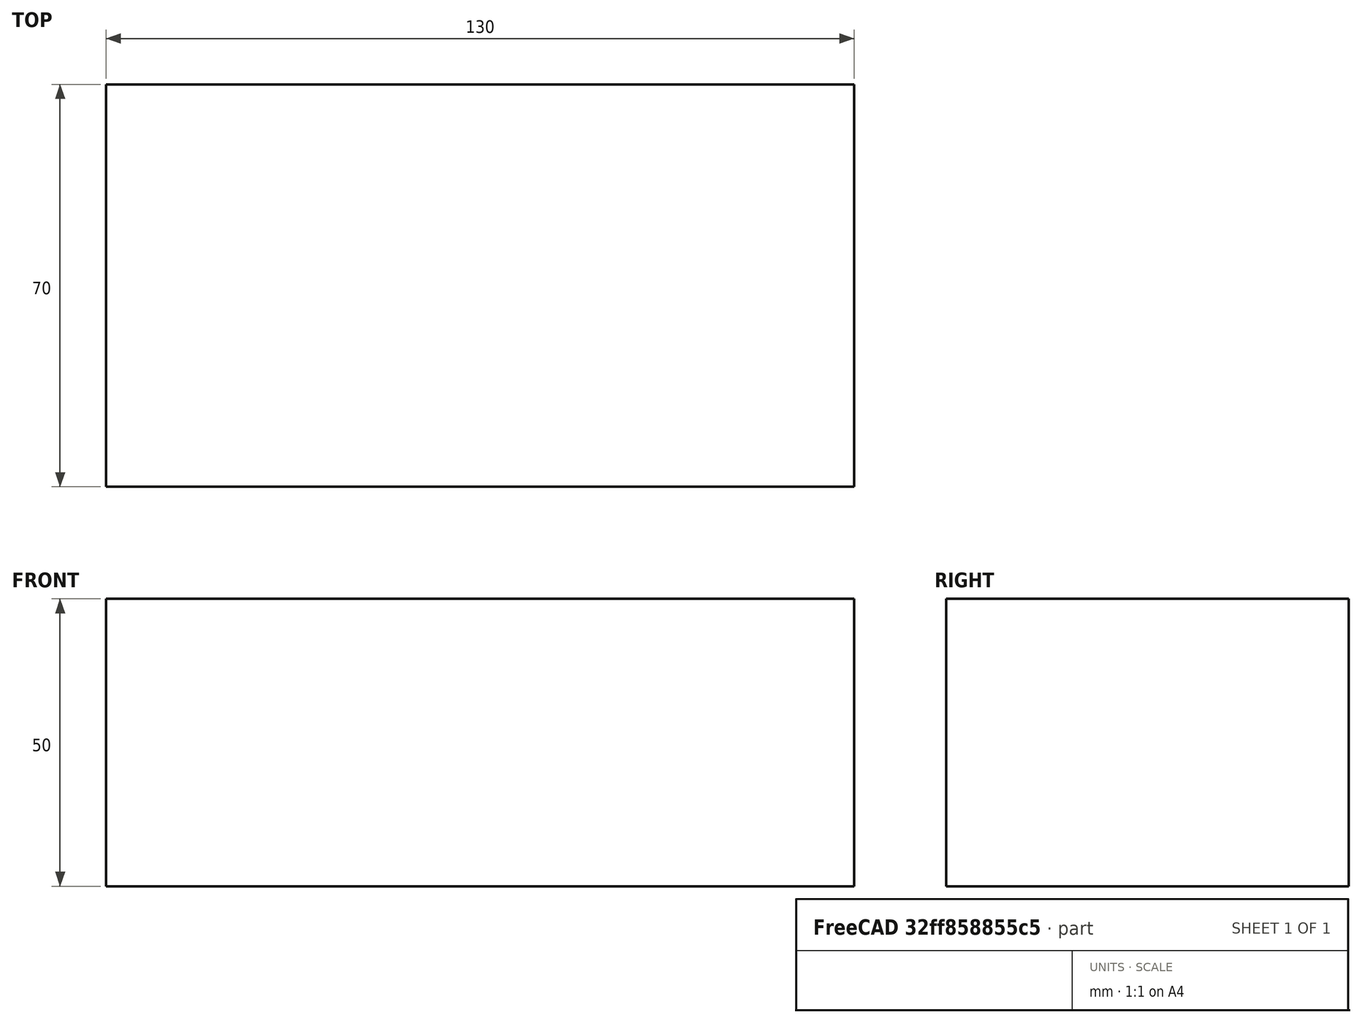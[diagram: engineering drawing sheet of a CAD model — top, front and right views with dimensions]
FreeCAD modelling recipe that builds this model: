
FCSTD DOCUMENT  (FreeCAD 0.15R4671 (Git))
Label: Flat Bar 130x70 EN10058 S235JR
License: All rights reserved
LicenseURL: http://en.wikipedia.org/wiki/All_rights_reserved
objects: Sketcher::SketchObject×1, Part::Extrusion×1
note: 2 computed .brp shape members not serialized (recipe doc carries the construction recipe); baked Part::Feature solids carry a one-line shape summary decoded from their .brp

FEATURE [Sketcher::SketchObject] Sketch
  sketch-geometry (4):
    g0: LineSegment StartX=-65 StartY=-35 StartZ=0 EndX=65 EndY=-35 EndZ=0
    g1: LineSegment StartX=65 StartY=-35 StartZ=0 EndX=65 EndY=35 EndZ=0
    g2: LineSegment StartX=65 StartY=35 StartZ=0 EndX=-65 EndY=35 EndZ=0
    g3: LineSegment StartX=-65 StartY=35 StartZ=0 EndX=-65 EndY=-35 EndZ=0
  constraints (12):
    c: Coincident(g0,g1)
    c: Coincident(g1,g2)
    c: Coincident(g2,g3)
    c: Coincident(g3,g0)
    c: Horizontal(g0)
    c: Horizontal(g2)
    c: Vertical(g1)
    c: Vertical(g3)
    c: Symmetric(g1,g2,g-2)
    c: Symmetric(g0,g1,g-1)
    c: DistanceY(g1) = 70
    c: DistanceX(g0) = 130
FEATURE [Part::Extrusion] Extrude  label="Flat Bar 130x70 EN10058 S235JR"
  Base = -> Sketch
  Dir = (0,0,50)
  Solid = true
